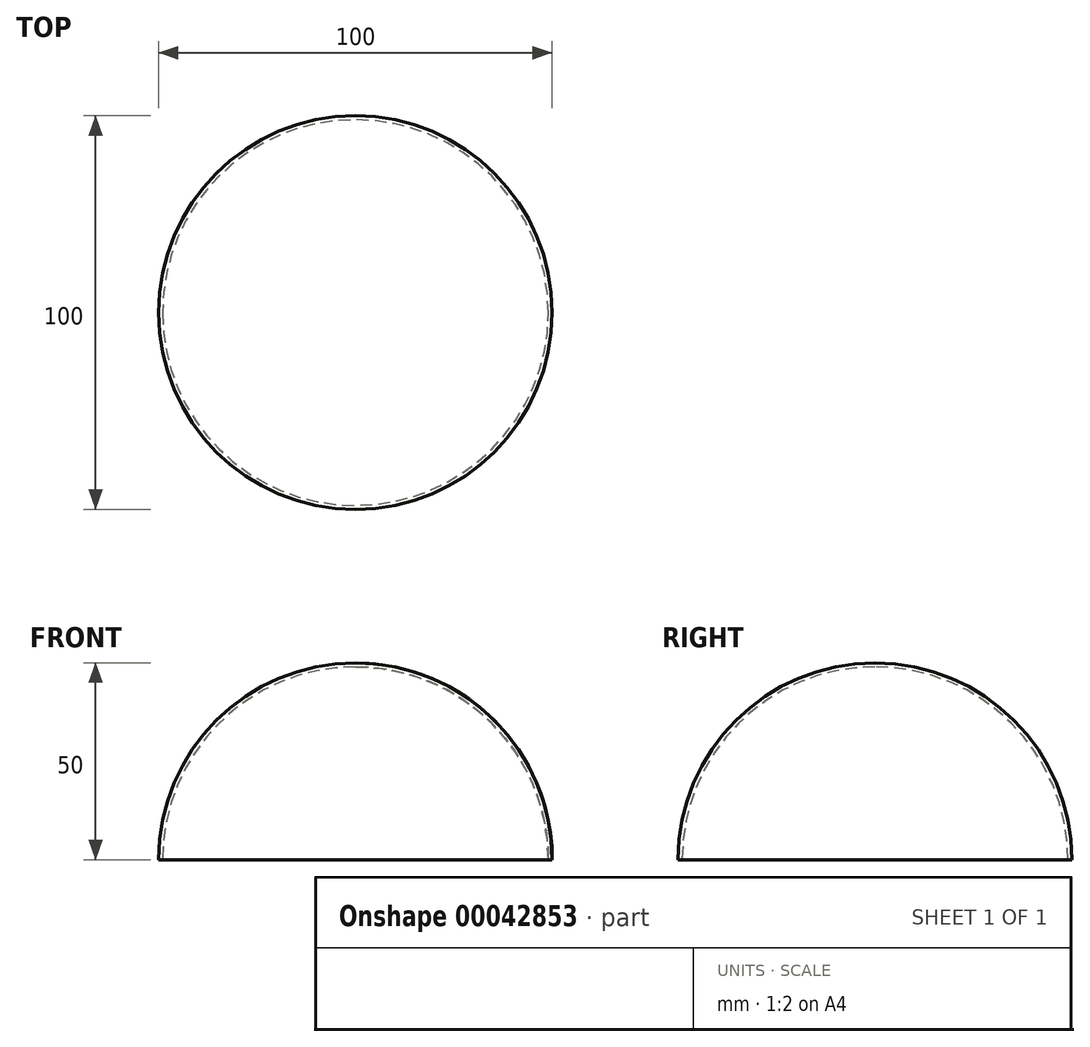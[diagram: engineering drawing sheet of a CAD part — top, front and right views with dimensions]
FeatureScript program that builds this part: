
annotation { "Feature Type Name" : "Feature", "Feature Type Description" : "" }
export const myFeature = defineFeature(function(context is Context, id is Id, definition is map)
    precondition{}
    {
        {
            var Q0;
            Q0=qCreatedBy(makeId("Front.planeOp"),FACE);
            var sketch = newSketch(context, id + "F0", { "sketchPlane" : qUnion([Q0])});
            skLineSegment(sketch, "E0", {"start": v(0, 0) * mm, "end": v(0, 50) * mm});
            skArc(sketch, "E1", {"start": v(50, 0) * mm, "mid": v(35.36, 35.36) * mm, "end": v(0, 50) * mm});
            skArc(sketch, "E2", {"start": v(49, 0) * mm, "mid": v(34.65, 34.65) * mm, "end": v(0, 49) * mm});
            skLineSegment(sketch, "E3", {"start": v(49, 0) * mm, "end": v(50, 0) * mm});
            skSolve(sketch);
        }
        {
            var Q0;
            Q0 = qSketchRegion(id + "F0", true);
            var Q1;
            Q1=sQuery(id+"F0.wireOp",EDGE,"E0");
            revolve(context, id + "F1", {"entities" : qUnion([Q0]), "axis" : qUnion([Q1]), "revolveType" : RevolveType.FULL});
        }
    });
